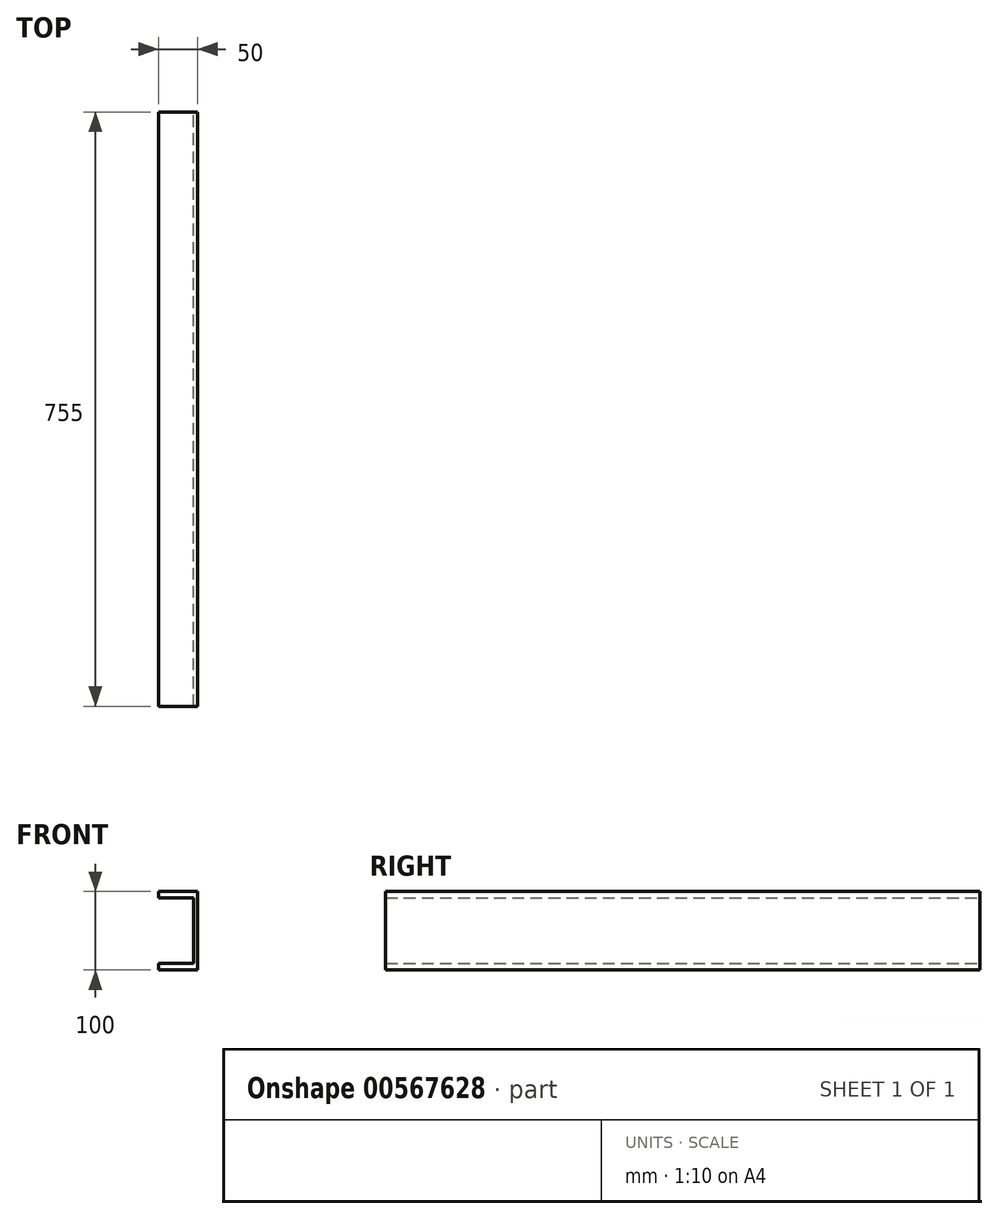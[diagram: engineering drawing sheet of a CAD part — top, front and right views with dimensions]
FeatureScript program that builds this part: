
annotation { "Feature Type Name" : "Feature", "Feature Type Description" : "" }
export const myFeature = defineFeature(function(context is Context, id is Id, definition is map)
    precondition{}
    {
        {
            var Q0;
            Q0=qCreatedBy(makeId("Front.planeOp"),FACE);
            var sketch = newSketch(context, id + "F0", { "sketchPlane" : qUnion([Q0])});
            skLineSegment(sketch, "E0", {"start": v(-45, 25.39) * mm, "end": v(5, 25.39) * mm});
            skLineSegment(sketch, "E1", {"start": v(5, 25.39) * mm, "end": v(5, -74.61) * mm});
            skLineSegment(sketch, "E2", {"start": v(5, -74.61) * mm, "end": v(-45, -74.61) * mm});
            skLineSegment(sketch, "E3", {"start": v(-45, -74.61) * mm, "end": v(-45, -66.11) * mm});
            skLineSegment(sketch, "E4", {"start": v(-45, -66.11) * mm, "end": v(0, -66.11) * mm});
            skLineSegment(sketch, "E5", {"start": v(0, -66.11) * mm, "end": v(0, 16.89) * mm});
            skLineSegment(sketch, "E6", {"start": v(0, 16.89) * mm, "end": v(-45, 16.89) * mm});
            skLineSegment(sketch, "E7", {"start": v(-45, 16.89) * mm, "end": v(-45, 25.39) * mm});
            skSolve(sketch);
        }
        {
            var Q0;
            Q0=makeQuery(id+"F0.imprint","IMPRINT",FACE,{"disambiguationData":[TD([[makeQuery(id+"F0.imprint","IMPRINT",EDGE,{"derivedFrom":sQuery(id+"F0.wireOp",EDGE,"E0")}),-1.0]])]});
            extrude(context, id + "F1", {"entities" : qUnion([Q0]), "depth" : 755 * mm, "offsetDistance" : 25 * mm});
        }
    });
